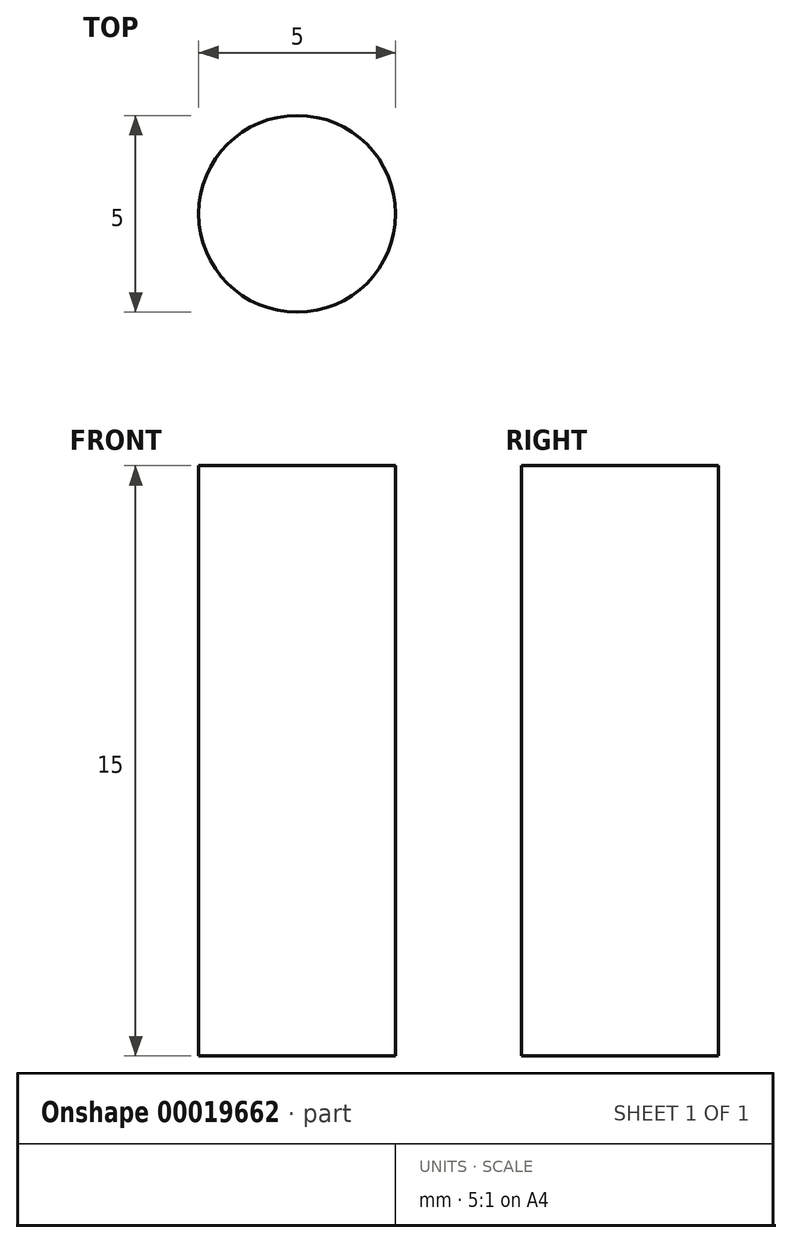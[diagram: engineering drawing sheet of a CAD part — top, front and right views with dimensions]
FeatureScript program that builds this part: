
annotation { "Feature Type Name" : "Feature", "Feature Type Description" : "" }
export const myFeature = defineFeature(function(context is Context, id is Id, definition is map)
    precondition{}
    {
        {
            var Q0;
            Q0=qCreatedBy(makeId("Top.planeOp"),FACE);
            var sketch = newSketch(context, id + "F0", { "sketchPlane" : qUnion([Q0])});
            skCircle(sketch, "E0", {"center": v(0, 0) * mm, "radius": 2.5 * mm});
            skSolve(sketch);
        }
        {
            var Q0;
            Q0=makeQuery(id+"F0.imprint","IMPRINT",FACE,{"disambiguationData":[TD([[makeQuery(id+"F0.imprint","IMPRINT",EDGE,{"derivedFrom":sQuery(id+"F0.wireOp",EDGE,"E0")}),1.0]])]});
            extrude(context, id + "F1", {"entities" : qUnion([Q0]), "depth" : 15 * mm});
        }
    });
